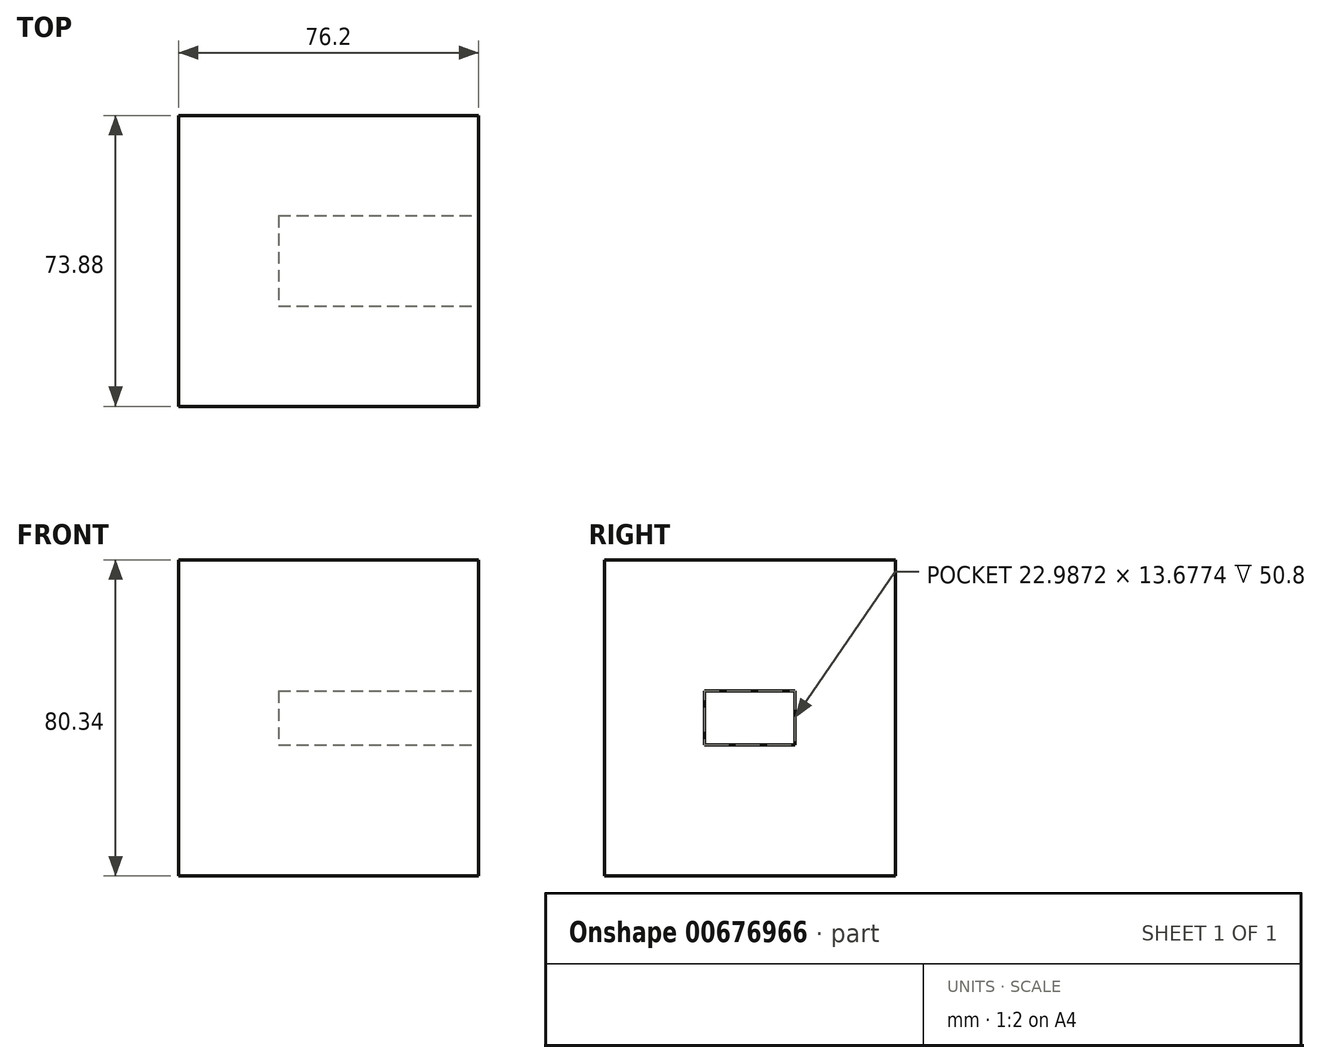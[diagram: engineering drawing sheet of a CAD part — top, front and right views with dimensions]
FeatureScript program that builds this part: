
annotation { "Feature Type Name" : "Feature", "Feature Type Description" : "" }
export const myFeature = defineFeature(function(context is Context, id is Id, definition is map)
    precondition{}
    {
        {
            var Q0;
            Q0=qCreatedBy(makeId("Right.planeOp"),FACE);
            var sketch = newSketch(context, id + "F0", { "sketchPlane" : qUnion([Q0])});
            skLineSegment(sketch, "E0.bottom", {"start": v(36.94, 40.17) * mm, "end": v(-36.94, 40.17) * mm});
            skLineSegment(sketch, "E0.top", {"start": v(36.94, -40.17) * mm, "end": v(-36.94, -40.17) * mm});
            skLineSegment(sketch, "E0.left", {"start": v(36.94, 40.17) * mm, "end": v(36.94, -40.17) * mm});
            skLineSegment(sketch, "E0.right", {"start": v(-36.94, 40.17) * mm, "end": v(-36.94, -40.17) * mm});
            skPoint(sketch, "E0.middle", {"position": v(0, 0) * mm});
            skSolve(sketch);
        }
        {
            var Q0;
            Q0 = qSketchRegion(id + "F0", true);
            extrude(context, id + "F1", {"entities" : qUnion([Q0]), "oppositeDirection" : true, "depth" : 76.2 * mm, "offsetDistance" : 25.4 * mm});
        }
        {
            var Q0;
            Q0=makeQuery(id+"F1.opExtrude","CAP_FACE",FACE,{"disambiguationData":[OSD([sQuery(id+"F0.wireOp",EDGE,"E0.bottom"),sQuery(id+"F0.wireOp",EDGE,"E0.top"),sQuery(id+"F0.wireOp",EDGE,"E0.left"),sQuery(id+"F0.wireOp",EDGE,"E0.right")])],"isStart":true});
            var sketch = newSketch(context, id + "F2", { "sketchPlane" : qUnion([Q0])});
            skLineSegment(sketch, "E1.bottom", {"start": v(11.5, 6.84) * mm, "end": v(-11.5, 6.84) * mm});
            skLineSegment(sketch, "E1.top", {"start": v(11.5, -6.84) * mm, "end": v(-11.5, -6.84) * mm});
            skLineSegment(sketch, "E1.left", {"start": v(11.5, 6.84) * mm, "end": v(11.5, -6.84) * mm});
            skLineSegment(sketch, "E1.right", {"start": v(-11.5, 6.84) * mm, "end": v(-11.5, -6.84) * mm});
            skPoint(sketch, "E1.middle", {"position": v(0, 0) * mm});
            skSolve(sketch);
        }
        {
            var Q0;
            Q0=makeQuery(id+"F2.imprint","IMPRINT",FACE,{"disambiguationData":[TD([[makeQuery(id+"F2.imprint","IMPRINT",EDGE,{"derivedFrom":sQuery(id+"F2.wireOp",EDGE,"E1.bottom")}),1.0]])]});
            extrude(context, id + "F3", {"entities" : qUnion([Q0]), "operationType" : NewBodyOperationType.REMOVE, "oppositeDirection" : true, "depth" : 50.8 * mm, "offsetDistance" : 25.4 * mm});
        }
    });
